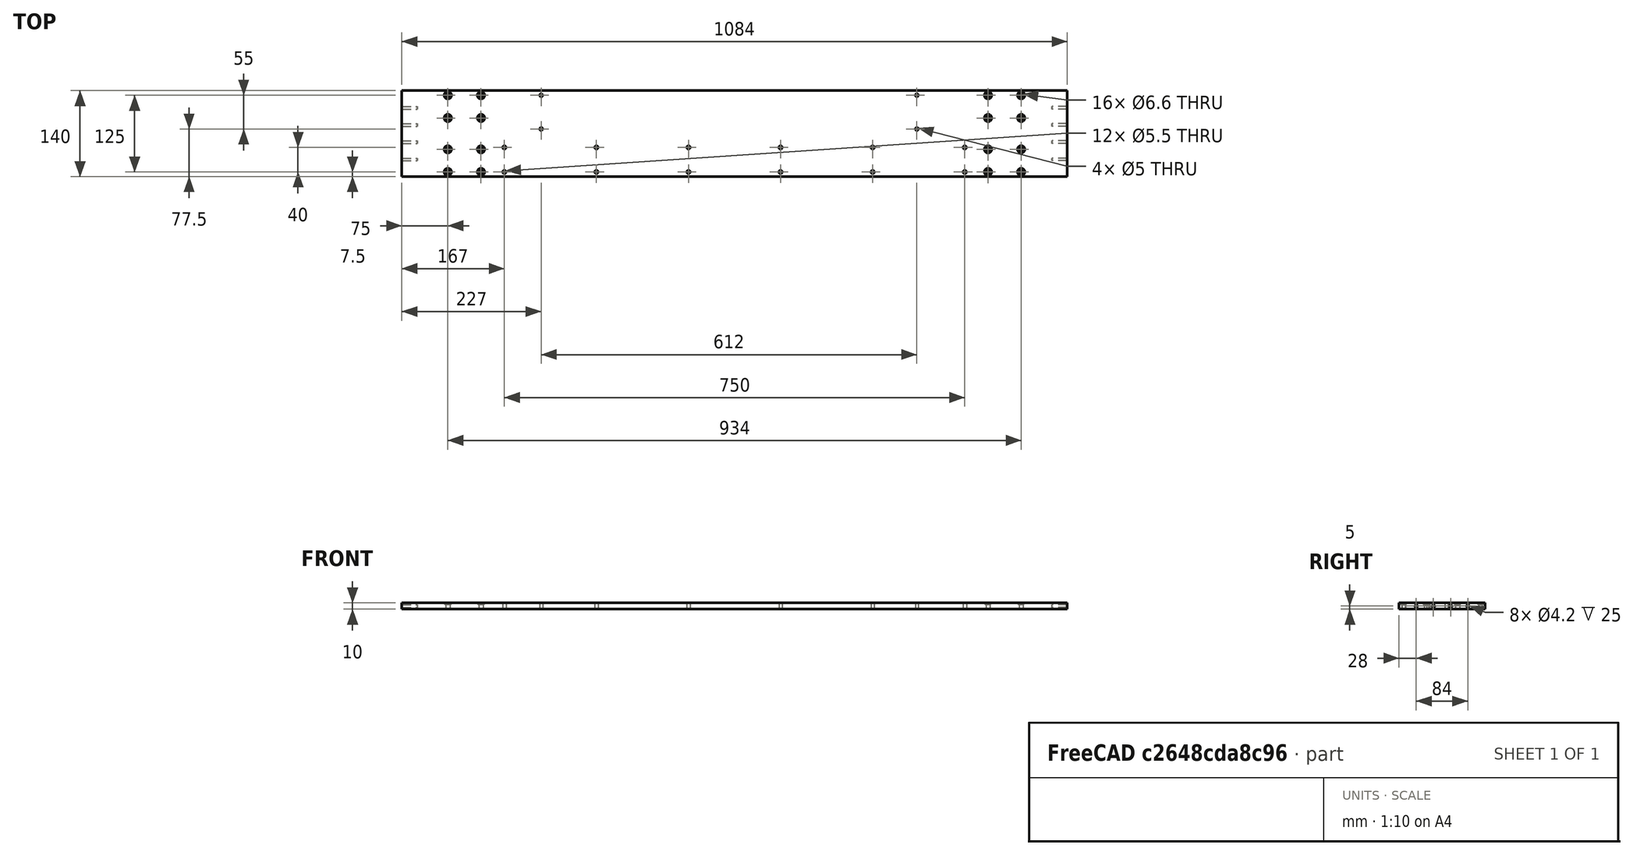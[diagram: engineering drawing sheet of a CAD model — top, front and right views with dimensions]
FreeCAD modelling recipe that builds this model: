
FCSTD DOCUMENT  (FreeCAD 0.17R13528 (Git))
Label: plate1
License: All rights reserved
LicenseURL: http://en.wikipedia.org/wiki/All_rights_reserved
objects: TechDraw::DrawViewDimension×32, PartDesign::LinearPattern×16, Sketcher::SketchObject×13, PartDesign::Hole×12, TechDraw::DrawProjGroupItem×2, PartDesign::Pad×1, PartDesign::Body×1, TechDraw::DrawSVGTemplate×1, TechDraw::DrawProjGroup×1, TechDraw::DrawViewAnnotation×1, TechDraw::DrawPage×1
note: 56 computed .brp shape members not serialized (recipe doc carries the construction recipe); baked Part::Feature solids carry a one-line shape summary decoded from their .brp

FEATURE [Sketcher::SketchObject] Sketch
  MapMode = 5
  Support = -> [XY_Plane]
  sketch-geometry (4):
    g0: LineSegment StartX=0 StartY=0 StartZ=0 EndX=1084 EndY=0 EndZ=0
    g1: LineSegment StartX=1084 StartY=0 StartZ=0 EndX=1084 EndY=140 EndZ=0
    g2: LineSegment StartX=1084 StartY=140 StartZ=0 EndX=0 EndY=140 EndZ=0
    g3: LineSegment StartX=0 StartY=140 StartZ=0 EndX=0 EndY=0 EndZ=0
  constraints (11):
    c: Coincident(g0,g1)
    c: Coincident(g1,g2)
    c: Coincident(g2,g3)
    c: Coincident(g3,g0)
    c: Horizontal(g0)
    c: Horizontal(g2)
    c: Vertical(g1)
    c: Vertical(g3)
    c: Coincident(g0,g-1)
    c: DistanceX(g0,g0) = 1084
    c: DistanceY(g3,g3) = 140
FEATURE [PartDesign::Pad] Pad
  Length = 10
  Length2 = 100
  Profile = -> Sketch
  Type = 0
FEATURE [Sketcher::SketchObject] Sketch001
  MapMode = 5
  Placement = pos=(0,0,10) rot=(0,0,1;0rad)
  Support = -> [Pad]
  sketch-geometry (1):
    g0: Circle CenterX=75 CenterY=7.5 CenterZ=0 NormalX=0 NormalY=0 NormalZ=1 AngleXU=0 Radius=10.4377
  constraints (2):
    c: Distance(g0,g-1) = 7.5
    c: Distance(g0,g-2) = 75
FEATURE [PartDesign::Hole] Hole
  BaseFeature = -> Pad
  Depth = 25
  DepthType = 1
  Diameter = 6.6
  DrillPoint = 0
  DrillPointAngle = 118
  HoleCutCountersinkAngle = 90
  HoleCutDepth = 0
  HoleCutDiameter = 12
  HoleCutType = 2
  ModelActualThread = false
  Profile = -> Sketch001
  Tapered = false
  TaperedAngle = 90
  ThreadAngle = 0
  ThreadClass = 0
  ThreadCutOffInner = 0
  ThreadCutOffOuter = 0
  ThreadDirection = 0
  ThreadFit = 0
  ThreadPitch = 0
  ThreadSize = 7
  ThreadType = 1
  Threaded = false
FEATURE [PartDesign::LinearPattern] LinearPattern
  BaseFeature = -> Hole
  Direction = -> Sketch001 [V_Axis]
  Length = 37
  Occurrences = 2
  Originals = -> [Hole]
FEATURE [PartDesign::LinearPattern] LinearPattern001
  BaseFeature = -> LinearPattern
  Direction = -> Sketch001 [V_Axis]
  Length = 88
  Occurrences = 2
  Originals = -> [Hole]
FEATURE [PartDesign::LinearPattern] LinearPattern002
  BaseFeature = -> LinearPattern001
  Direction = -> Sketch001 [V_Axis]
  Length = 125
  Occurrences = 2
  Originals = -> [Hole]
FEATURE [Sketcher::SketchObject] Sketch002
  MapMode = 5
  Placement = pos=(0,0,10) rot=(0,0,1;0rad)
  Support = -> [LinearPattern002]
  sketch-geometry (1):
    g0: Circle CenterX=129 CenterY=7.5 CenterZ=0 NormalX=0 NormalY=0 NormalZ=1 AngleXU=0 Radius=9.61982
  constraints (2):
    c: Distance(g0,g-1) = 7.5
    c: Distance(g0,g-2) = 129
FEATURE [PartDesign::Hole] Hole001
  BaseFeature = -> LinearPattern002
  Depth = 25
  DepthType = 1
  Diameter = 6.6
  DrillPoint = 0
  DrillPointAngle = 118
  HoleCutCountersinkAngle = 90
  HoleCutDepth = 0
  HoleCutDiameter = 12
  HoleCutType = 2
  ModelActualThread = false
  Profile = -> Sketch002
  Tapered = false
  TaperedAngle = 90
  ThreadAngle = 0
  ThreadClass = 0
  ThreadCutOffInner = 0
  ThreadCutOffOuter = 0
  ThreadDirection = 0
  ThreadFit = 0
  ThreadPitch = 0
  ThreadSize = 7
  ThreadType = 1
  Threaded = false
FEATURE [PartDesign::LinearPattern] LinearPattern003
  BaseFeature = -> Hole001
  Direction = -> Sketch002 [V_Axis]
  Length = 37
  Occurrences = 2
  Originals = -> [Hole001]
FEATURE [PartDesign::LinearPattern] LinearPattern004
  BaseFeature = -> LinearPattern003
  Direction = -> Sketch002 [V_Axis]
  Length = 88
  Occurrences = 2
  Originals = -> [Hole001]
FEATURE [PartDesign::LinearPattern] LinearPattern005
  BaseFeature = -> LinearPattern004
  Direction = -> Sketch002 [V_Axis]
  Length = 125
  Occurrences = 2
  Originals = -> [Hole001]
FEATURE [Sketcher::SketchObject] Sketch003
  MapMode = 5
  Placement = pos=(0,0,10) rot=(0,0,1;0rad)
  Support = -> [LinearPattern005]
  sketch-geometry (1):
    g0: Circle CenterX=167 CenterY=7.5 CenterZ=0 NormalX=0 NormalY=0 NormalZ=1 AngleXU=0 Radius=18.1762
  constraints (2):
    c: Distance(g0,g-1) = 7.5
    c: Distance(g0,g-2) = 167
FEATURE [PartDesign::Hole] Hole002
  BaseFeature = -> LinearPattern005
  Depth = 25
  DepthType = 1
  Diameter = 5.5
  DrillPoint = 0
  DrillPointAngle = 118
  HoleCutCountersinkAngle = 90
  HoleCutDepth = 0
  HoleCutDiameter = 5
  HoleCutType = 0
  ModelActualThread = false
  Profile = -> Sketch003
  Tapered = false
  TaperedAngle = 90
  ThreadAngle = 0
  ThreadClass = 0
  ThreadCutOffInner = 0
  ThreadCutOffOuter = 0
  ThreadDirection = 0
  ThreadFit = 0
  ThreadPitch = 0
  ThreadSize = 6
  ThreadType = 1
  Threaded = false
FEATURE [PartDesign::LinearPattern] LinearPattern006
  BaseFeature = -> Hole002
  Direction = -> Sketch003 [H_Axis]
  Length = 750
  Occurrences = 6
  Originals = -> [Hole002]
FEATURE [Sketcher::SketchObject] Sketch004
  MapMode = 5
  Placement = pos=(0,0,10) rot=(0,0,1;0rad)
  Support = -> [LinearPattern006]
  sketch-geometry (1):
    g0: Circle CenterX=167 CenterY=47.5 CenterZ=0 NormalX=0 NormalY=0 NormalZ=1 AngleXU=0 Radius=11.8826
  constraints (2):
    c: Distance(g0,g-1) = 47.5
    c: Distance(g0,g-2) = 167
FEATURE [PartDesign::Hole] Hole003
  BaseFeature = -> LinearPattern006
  Depth = 25
  DepthType = 1
  Diameter = 5.5
  DrillPoint = 0
  DrillPointAngle = 118
  HoleCutCountersinkAngle = 90
  HoleCutDepth = 0
  HoleCutDiameter = 5
  HoleCutType = 0
  ModelActualThread = false
  Profile = -> Sketch004
  Tapered = false
  TaperedAngle = 90
  ThreadAngle = 0
  ThreadClass = 0
  ThreadCutOffInner = 0
  ThreadCutOffOuter = 0
  ThreadDirection = 0
  ThreadFit = 0
  ThreadPitch = 0
  ThreadSize = 6
  ThreadType = 1
  Threaded = false
FEATURE [PartDesign::LinearPattern] LinearPattern007
  BaseFeature = -> Hole003
  Direction = -> Sketch004 [H_Axis]
  Length = 750
  Occurrences = 6
  Originals = -> [Hole003]
FEATURE [Sketcher::SketchObject] Sketch005
  MapMode = 5
  Placement = pos=(0,0,10) rot=(0,0,1;0rad)
  Support = -> [LinearPattern007]
  sketch-geometry (1):
    g0: Circle CenterX=227 CenterY=132.5 CenterZ=0 NormalX=0 NormalY=0 NormalZ=1 AngleXU=0 Radius=12.3627
  constraints (2):
    c: Distance(g0,g-1) = 132.5
    c: Distance(g0,g-2) = 227
FEATURE [PartDesign::Hole] Hole004
  BaseFeature = -> LinearPattern007
  Depth = 25
  DepthType = 1
  Diameter = 5
  DrillPoint = 0
  DrillPointAngle = 118
  HoleCutCountersinkAngle = 90
  HoleCutDepth = 0
  HoleCutDiameter = 6
  HoleCutType = 0
  ModelActualThread = false
  Profile = -> Sketch005
  Tapered = false
  TaperedAngle = 90
  ThreadAngle = 60
  ThreadClass = 0
  ThreadCutOffInner = 0.108253
  ThreadCutOffOuter = 0.216506
  ThreadDirection = 1
  ThreadFit = 0
  ThreadPitch = 1
  ThreadSize = 7
  ThreadType = 1
  Threaded = true
FEATURE [PartDesign::LinearPattern] LinearPattern008
  BaseFeature = -> Hole004
  Direction = -> Sketch005 [H_Axis]
  Length = 612
  Occurrences = 2
  Originals = -> [Hole004]
FEATURE [Sketcher::SketchObject] Sketch006
  MapMode = 5
  Placement = pos=(0,0,10) rot=(0,0,1;0rad)
  Support = -> [LinearPattern008]
  sketch-geometry (1):
    g0: Circle CenterX=227 CenterY=77.5 CenterZ=0 NormalX=0 NormalY=0 NormalZ=1 AngleXU=0 Radius=12.7181
  constraints (2):
    c: Distance(g0,g-1) = 77.5
    c: Distance(g0,g-2) = 227
FEATURE [PartDesign::Hole] Hole005
  BaseFeature = -> LinearPattern008
  Depth = 25
  DepthType = 1
  Diameter = 5
  DrillPoint = 0
  DrillPointAngle = 118
  HoleCutCountersinkAngle = 90
  HoleCutDepth = 0
  HoleCutDiameter = 6
  HoleCutType = 0
  ModelActualThread = false
  Profile = -> Sketch006
  Tapered = false
  TaperedAngle = 90
  ThreadAngle = 60
  ThreadClass = 0
  ThreadCutOffInner = 0.108253
  ThreadCutOffOuter = 0.216506
  ThreadDirection = 1
  ThreadFit = 0
  ThreadPitch = 1
  ThreadSize = 7
  ThreadType = 1
  Threaded = true
FEATURE [PartDesign::LinearPattern] LinearPattern009
  BaseFeature = -> Hole005
  Direction = -> Sketch006 [H_Axis]
  Length = 612
  Occurrences = 2
  Originals = -> [Hole005]
FEATURE [Sketcher::SketchObject] Sketch007
  MapMode = 5
  Placement = pos=(0,0,10) rot=(0,0,1;0rad)
  Support = -> [LinearPattern009]
  sketch-geometry (1):
    g0: Circle CenterX=1009 CenterY=132.5 CenterZ=0 NormalX=0 NormalY=0 NormalZ=1 AngleXU=0 Radius=17.4662
  constraints (2):
    c: Distance(g0,g-2) = 1009
    c: Distance(g0,g-1) = 132.5
FEATURE [PartDesign::Hole] Hole006
  BaseFeature = -> LinearPattern009
  Depth = 25
  DepthType = 1
  Diameter = 6.6
  DrillPoint = 0
  DrillPointAngle = 118
  HoleCutCountersinkAngle = 90
  HoleCutDepth = 0
  HoleCutDiameter = 12
  HoleCutType = 2
  ModelActualThread = false
  Profile = -> Sketch007
  Tapered = false
  TaperedAngle = 90
  ThreadAngle = 0
  ThreadClass = 0
  ThreadCutOffInner = 0
  ThreadCutOffOuter = 0
  ThreadDirection = 0
  ThreadFit = 0
  ThreadPitch = 0
  ThreadSize = 7
  ThreadType = 1
  Threaded = false
FEATURE [PartDesign::LinearPattern] LinearPattern010
  BaseFeature = -> Hole006
  Direction = -> Sketch007 [H_Axis]
  Length = 54
  Occurrences = 2
  Originals = -> [Hole006]
  Reversed = true
FEATURE [Sketcher::SketchObject] Sketch008
  MapMode = 5
  Placement = pos=(0,0,10) rot=(0,0,1;0rad)
  Support = -> [LinearPattern010]
  sketch-geometry (1):
    g0: Circle CenterX=1009 CenterY=95.5 CenterZ=0 NormalX=0 NormalY=0 NormalZ=1 AngleXU=0 Radius=18.6644
  constraints (2):
    c: Distance(g0,g-2) = 1009
    c: Distance(g0,g-1) = 95.5
FEATURE [PartDesign::Hole] Hole007
  BaseFeature = -> LinearPattern010
  Depth = 25
  DepthType = 1
  Diameter = 6.6
  DrillPoint = 0
  DrillPointAngle = 118
  HoleCutCountersinkAngle = 90
  HoleCutDepth = 0
  HoleCutDiameter = 12
  HoleCutType = 2
  ModelActualThread = false
  Profile = -> Sketch008
  Tapered = false
  TaperedAngle = 90
  ThreadAngle = 0
  ThreadClass = 0
  ThreadCutOffInner = 0
  ThreadCutOffOuter = 0
  ThreadDirection = 0
  ThreadFit = 0
  ThreadPitch = 0
  ThreadSize = 7
  ThreadType = 1
  Threaded = false
FEATURE [PartDesign::LinearPattern] LinearPattern011
  BaseFeature = -> Hole007
  Direction = -> Sketch008 [H_Axis]
  Length = 54
  Occurrences = 2
  Originals = -> [Hole007]
  Reversed = true
FEATURE [Sketcher::SketchObject] Sketch009
  MapMode = 5
  Placement = pos=(0,0,10) rot=(0,0,1;0rad)
  Support = -> [LinearPattern011]
  sketch-geometry (1):
    g0: Circle CenterX=1009 CenterY=7.5 CenterZ=0 NormalX=0 NormalY=0 NormalZ=1 AngleXU=0 Radius=11.8629
  constraints (2):
    c: Distance(g0,g-2) = 1009
    c: Distance(g0,g-1) = 7.5
FEATURE [PartDesign::Hole] Hole008
  BaseFeature = -> LinearPattern011
  Depth = 25
  DepthType = 1
  Diameter = 6.6
  DrillPoint = 0
  DrillPointAngle = 118
  HoleCutCountersinkAngle = 90
  HoleCutDepth = 0
  HoleCutDiameter = 12
  HoleCutType = 2
  ModelActualThread = false
  Profile = -> Sketch009
  Tapered = false
  TaperedAngle = 90
  ThreadAngle = 0
  ThreadClass = 0
  ThreadCutOffInner = 0
  ThreadCutOffOuter = 0
  ThreadDirection = 0
  ThreadFit = 0
  ThreadPitch = 0
  ThreadSize = 7
  ThreadType = 1
  Threaded = false
FEATURE [PartDesign::LinearPattern] LinearPattern012
  BaseFeature = -> Hole008
  Direction = -> Sketch009 [H_Axis]
  Length = 54
  Occurrences = 2
  Originals = -> [Hole008]
  Reversed = true
FEATURE [Sketcher::SketchObject] Sketch010
  MapMode = 5
  Placement = pos=(0,0,10) rot=(0,0,1;0rad)
  Support = -> [LinearPattern012]
  sketch-geometry (1):
    g0: Circle CenterX=1009 CenterY=44.5 CenterZ=0 NormalX=0 NormalY=0 NormalZ=1 AngleXU=0 Radius=7.99747
  constraints (2):
    c: Distance(g0,g-2) = 1009
    c: Distance(g0,g-1) = 44.5
FEATURE [PartDesign::Hole] Hole009
  BaseFeature = -> LinearPattern012
  Depth = 25
  DepthType = 1
  Diameter = 6.6
  DrillPoint = 0
  DrillPointAngle = 118
  HoleCutCountersinkAngle = 90
  HoleCutDepth = 0
  HoleCutDiameter = 12
  HoleCutType = 2
  ModelActualThread = false
  Profile = -> Sketch010
  Tapered = false
  TaperedAngle = 90
  ThreadAngle = 0
  ThreadClass = 0
  ThreadCutOffInner = 0
  ThreadCutOffOuter = 0
  ThreadDirection = 0
  ThreadFit = 0
  ThreadPitch = 0
  ThreadSize = 7
  ThreadType = 1
  Threaded = false
FEATURE [PartDesign::LinearPattern] LinearPattern013
  BaseFeature = -> Hole009
  Direction = -> Sketch010 [H_Axis]
  Length = 54
  Occurrences = 2
  Originals = -> [Hole009]
  Reversed = true
FEATURE [Sketcher::SketchObject] Sketch011
  MapMode = 5
  Placement = pos=(0,0,0) rot=(0.57735,-0.57735,-0.57735;2.0944rad)
  Support = -> [LinearPattern013]
  sketch-geometry (1):
    g0: Circle CenterX=-28 CenterY=5 CenterZ=0 NormalX=0 NormalY=0 NormalZ=1 AngleXU=0 Radius=5.00486
  constraints (2):
    c: Distance(g0,g-1) = 5
    c: Distance(g0,g-2) = 28
FEATURE [PartDesign::Hole] Hole010
  BaseFeature = -> LinearPattern013
  Depth = 25
  DepthType = 0
  Diameter = 4.2
  DrillPoint = 0
  DrillPointAngle = 118
  HoleCutCountersinkAngle = 90
  HoleCutDepth = 0
  HoleCutDiameter = 5
  HoleCutType = 0
  ModelActualThread = false
  Profile = -> Sketch011
  Tapered = false
  TaperedAngle = 90
  ThreadAngle = 60
  ThreadClass = 0
  ThreadCutOffInner = 0.0866025
  ThreadCutOffOuter = 0.173205
  ThreadDirection = 1
  ThreadFit = 0
  ThreadPitch = 0.8
  ThreadSize = 6
  ThreadType = 1
  Threaded = true
FEATURE [PartDesign::LinearPattern] LinearPattern014
  BaseFeature = -> Hole010
  Direction = -> Sketch011 [H_Axis]
  Length = 84
  Occurrences = 4
  Originals = -> [Hole010]
  Reversed = true
FEATURE [Sketcher::SketchObject] Sketch012
  MapMode = 5
  Placement = pos=(1084,0,0) rot=(0.57735,0.57735,0.57735;2.0944rad)
  Support = -> [LinearPattern014]
  sketch-geometry (1):
    g0: Circle CenterX=28 CenterY=5 CenterZ=0 NormalX=0 NormalY=0 NormalZ=1 AngleXU=0 Radius=2.71805
  constraints (2):
    c: Distance(g0,g-2) = 28
    c: Distance(g0,g-1) = 5
FEATURE [PartDesign::Hole] Hole011
  BaseFeature = -> LinearPattern014
  Depth = 25
  DepthType = 0
  Diameter = 4.2
  DrillPoint = 0
  DrillPointAngle = 118
  HoleCutCountersinkAngle = 90
  HoleCutDepth = 0
  HoleCutDiameter = 5
  HoleCutType = 0
  ModelActualThread = false
  Profile = -> Sketch012
  Tapered = false
  TaperedAngle = 90
  ThreadAngle = 60
  ThreadClass = 0
  ThreadCutOffInner = 0.0866025
  ThreadCutOffOuter = 0.173205
  ThreadDirection = 1
  ThreadFit = 0
  ThreadPitch = 0.8
  ThreadSize = 6
  ThreadType = 1
  Threaded = true
FEATURE [PartDesign::LinearPattern] LinearPattern015
  BaseFeature = -> Hole011
  Direction = -> Sketch012 [H_Axis]
  Length = 84
  Occurrences = 4
  Originals = -> [Hole011]
FEATURE [PartDesign::Body] Body
  Group = -> [Sketch,Pad,Sketch001,Hole,LinearPattern,LinearPattern001,LinearPattern002,Sketch002,Hole001,LinearPattern003,LinearPattern004,LinearPattern005,Sketch003,Hole002,LinearPattern006,Sketch004,Hole003,LinearPattern007,Sketch005,Hole004,LinearPattern008,Sketch006,Hole005,LinearPattern009,Sketch007,Hole006,LinearPattern010,Sketch008,Hole007,LinearPattern011,Sketch009,Hole008,LinearPattern012,Sketch010,+8 more]
  Origin = -> Origin
  Tip = -> LinearPattern015
FEATURE [TechDraw::DrawSVGTemplate] Template
  EditableTexts = Designed_by_Name=Lukas Winter; FC-Date=27.08.2018; FC-SC=1:4; FC-SH=1/2; FC-Title=COSI Measure v1.0; Subtitle=Mechanical assembly - plate 1
  Height = 210
  Orientation = 1
  Width = 297
FEATURE [TechDraw::DrawProjGroupItem] ProjItem  label="Front"
  CoarseView = false
  Direction = (0,0,-1)
  Focus = 100
  HardHidden = false
  IsoCount = 0
  IsoHidden = false
  IsoVisible = false
  LockPosition = false
  Perspective = false
  Rotation = 0
  RotationVector = (1,0,0)
  ScaleType = 0
  SeamHidden = false
  SeamVisible = false
  SmoothHidden = false
  SmoothVisible = false
  Source = -> [Body]
  Type = 0
  X = 0
  Y = -32.5
FEATURE [TechDraw::DrawProjGroupItem] ProjItem001  label="Top"
  CoarseView = false
  Direction = (0,-1,0)
  Focus = 100
  HardHidden = false
  IsoCount = 0
  IsoHidden = false
  IsoVisible = false
  LockPosition = false
  Perspective = false
  Rotation = 0
  RotationVector = (1,0,0)
  Scale = 0.125
  ScaleType = 2
  SeamHidden = false
  SeamVisible = false
  SmoothHidden = false
  SmoothVisible = false
  Source = -> [Body]
  Type = 4
  X = 0
  Y = -50
FEATURE [TechDraw::DrawProjGroup] ProjGroup
  Anchor = -> ProjItem
  AutoDistribute = true
  CubeDirs = (6) [(-1.22465e-16,1,-1.83697e-16),(1.98248e-32,-1.83697e-16,-1),(-1,-1.22465e-16,2.67165e-33),(-1.98248e-32,1.83697e-16,1),(1,1.22465e-16,-2.67165e-33),(1.22465e-16,-1,1.83697e-16)]
  CubeRotations = (6) [(1,1.22465e-16,-2.44929e-16),(1,1.22465e-16,-2.44929e-16),(4.89859e-16,1.83697e-16,-1),(-1,-1.22465e-16,2.44929e-16),(-4.89859e-16,-1.83697e-16,1),(1,1.22465e-16,-2.44929e-16)]
  LockPosition = false
  ProjectionType = 0
  Rotation = 0
  Scale = 0.25
  ScaleType = 2
  Source = -> [Body]
  Views = -> [ProjItem,ProjItem001]
  X = 148.275
  Y = 143.647
  spacingX = 15
  spacingY = 15
FEATURE [TechDraw::DrawViewDimension] Dimension
  FormatSpec = %.2f
  LockPosition = false
  MeasureType = 1
  References2D = -> [ProjItem001]
  Rotation = 0
  ScaleType = 0
  Type = 1
  X = -1.86667
  Y = -14
FEATURE [TechDraw::DrawViewDimension] Dimension001
  FormatSpec = %.2f
  LockPosition = false
  MeasureType = 1
  References2D = -> [ProjItem001]
  Rotation = 0
  ScaleType = 0
  Type = 2
  X = -45.1111
  Y = -31.8889
FEATURE [TechDraw::DrawViewDimension] Dimension013
  FormatSpec = %.2f
  LockPosition = false
  MeasureType = 1
  References2D = -> [ProjItem]
  Rotation = 0
  ScaleType = 0
  Type = 1
  X = -107.531
  Y = 28.469
FEATURE [TechDraw::DrawViewDimension] Dimension014
  FormatSpec = %.2f
  LockPosition = false
  MeasureType = 1
  References2D = -> [ProjItem]
  Rotation = 0
  ScaleType = 0
  Type = 1
  X = -124.963
  Y = 36.8148
FEATURE [TechDraw::DrawViewDimension] Dimension020
  FormatSpec = %.2f
  LockPosition = false
  MeasureType = 1
  References2D = -> [ProjItem]
  Rotation = 0
  ScaleType = 0
  Type = 1
  X = -92.7648
  Y = 39.8882
FEATURE [TechDraw::DrawViewDimension] Dimension024
  FormatSpec = %.2f
  LockPosition = false
  MeasureType = 1
  References2D = -> [ProjItem]
  Rotation = 0
  ScaleType = 0
  Type = 2
  X = -90.4522
  Y = -6.07601
FEATURE [TechDraw::DrawViewDimension] Dimension026
  FormatSpec = %.2f
  LockPosition = false
  MeasureType = 1
  References2D = -> [ProjItem]
  Rotation = 0
  ScaleType = 0
  Type = 2
  X = 7.78062
  Y = 7.66924
FEATURE [TechDraw::DrawViewDimension] Dimension027
  FormatSpec = %.2f
  LockPosition = false
  MeasureType = 1
  References2D = -> [ProjItem]
  Rotation = 0
  ScaleType = 0
  Type = 2
  X = 123.504
  Y = -1.77713
FEATURE [TechDraw::DrawViewDimension] Dimension029
  FormatSpec = %.2f
  LockPosition = false
  MeasureType = 1
  References2D = -> [ProjItem]
  Rotation = 0
  ScaleType = 0
  Type = 2
  X = 130.528
  Y = 5.79369
FEATURE [TechDraw::DrawViewAnnotation] Annotation
  Font = osifont
  LineSpace = 80
  LockPosition = false
  MaxWidth = -1
  Rotation = 0
  ScaleType = 0
  Text = The 12 holes in the center top (Front view)  | are for M5 bolts (d=5.5mm). All other holes are | for M6 screws.  | Make countersinks (16x) for the d=6.6mm holes. | Make M6 threads (4x) for the d=5mm holes.
  TextSize = 2.8
  TextStyle = 0
  X = 150.571
  Y = 187.55
FEATURE [TechDraw::DrawViewDimension] Dimension038
  FormatSpec = %.2f
  LockPosition = false
  MeasureType = 1
  References2D = -> [ProjItem]
  Rotation = 0
  ScaleType = 0
  Type = 2
  X = 25.6282
  Y = -0.366117
FEATURE [TechDraw::DrawViewDimension] Dimension039
  FormatSpec = %.2f
  LockPosition = false
  MeasureType = 1
  References2D = -> [ProjItem]
  Rotation = 0
  ScaleType = 0
  Type = 1
  X = 126.382
  Y = 34.3645
FEATURE [TechDraw::DrawViewDimension] Dimension040
  FormatSpec = %.2f
  LockPosition = false
  MeasureType = 1
  References2D = -> [ProjItem]
  Rotation = 0
  ScaleType = 0
  Type = 1
  X = -68.729
  Y = 26.4124
FEATURE [TechDraw::DrawViewDimension] Dimension041
  FormatSpec = %.2f
  LockPosition = false
  MeasureType = 1
  References2D = -> [ProjItem]
  Rotation = 0
  ScaleType = 0
  Type = 1
  X = -38.3406
  Y = 26.4124
FEATURE [TechDraw::DrawViewDimension] Dimension042
  FormatSpec = %.2f
  LockPosition = false
  MeasureType = 1
  References2D = -> [ProjItem]
  Rotation = 0
  ScaleType = 0
  Type = 1
  X = -1.13602
  Y = 26.1284
FEATURE [TechDraw::DrawViewDimension] Dimension043
  FormatSpec = %.2f
  LockPosition = false
  MeasureType = 1
  References2D = -> [ProjItem]
  Rotation = 0
  ScaleType = 0
  Type = 1
  X = 39.4766
  Y = 25.8444
FEATURE [TechDraw::DrawViewDimension] Dimension044
  FormatSpec = %.2f
  LockPosition = false
  MeasureType = 1
  References2D = -> [ProjItem]
  Rotation = 0
  ScaleType = 0
  Type = 1
  X = 76.1131
  Y = 25.5604
FEATURE [TechDraw::DrawViewDimension] Dimension045
  FormatSpec = %.2f
  LockPosition = false
  MeasureType = 1
  References2D = -> [ProjItem]
  Rotation = 0
  ScaleType = 0
  Type = 2
  X = -128.086
  Y = -8.23612
FEATURE [TechDraw::DrawViewDimension] Dimension046
  FormatSpec = %.2f
  LockPosition = false
  MeasureType = 1
  References2D = -> [ProjItem]
  Rotation = 0
  ScaleType = 0
  Type = 2
  X = -132.63
  Y = 6.5321
FEATURE [TechDraw::DrawViewDimension] Dimension047
  FormatSpec = %.2f
  LockPosition = false
  MeasureType = 1
  References2D = -> [ProjItem]
  Rotation = 0
  ScaleType = 0
  Type = 2
  X = -114.454
  Y = 4.82807
FEATURE [TechDraw::DrawViewDimension] Dimension048
  FormatSpec = %.2f
  LockPosition = false
  MeasureType = 1
  References2D = -> [ProjItem]
  Rotation = 0
  ScaleType = 0
  Type = 1
  X = -107.07
  Y = -32.0925
FEATURE [TechDraw::DrawViewDimension] Dimension049
  FormatSpec = %.2f
  LockPosition = false
  MeasureType = 1
  References2D = -> [ProjItem]
  Rotation = 0
  ScaleType = 0
  Type = 1
  X = -0.284004
  Y = -32.3765
FEATURE [TechDraw::DrawViewDimension] Dimension050
  FormatSpec = %.2f
  LockPosition = false
  MeasureType = 1
  References2D = -> [ProjItem]
  Rotation = 0
  ScaleType = 0
  Type = 2
  X = 66.741
  Y = -4.26006
FEATURE [TechDraw::DrawViewDimension] Dimension051
  FormatSpec = %.2f
  LockPosition = false
  MeasureType = 1
  References2D = -> [ProjItem]
  Rotation = 0
  ScaleType = 0
  Type = 2
  X = -72.7051
  Y = -5.11208
FEATURE [TechDraw::DrawViewDimension] Dimension052
  FormatSpec = %.2f
  LockPosition = false
  MeasureType = 1
  References2D = -> [ProjItem]
  Rotation = 0
  ScaleType = 0
  Type = 1
  X = 100.538
  Y = 38.9086
FEATURE [TechDraw::DrawViewDimension] Dimension053
  FormatSpec = %.2f
  LockPosition = false
  MeasureType = 1
  References2D = -> [ProjItem]
  Rotation = 0
  ScaleType = 0
  Type = 1
  X = 113.602
  Y = 28.1164
FEATURE [TechDraw::DrawViewDimension] Dimension054
  FormatSpec = %.2f
  LockPosition = false
  MeasureType = 1
  References2D = -> [ProjItem]
  Rotation = 0
  ScaleType = 0
  Type = 2
  X = 95.9934
  Y = -6.24809
FEATURE [TechDraw::DrawViewDimension] Dimension055
  FormatSpec = %.2f
  LockPosition = false
  MeasureType = 1
  References2D = -> [ProjItem]
  Rotation = 0
  ScaleType = 0
  Type = 5
  X = -10.5024
  Y = -6.00137
FEATURE [TechDraw::DrawViewDimension] Dimension056
  FormatSpec = %.2f
  LockPosition = false
  MeasureType = 1
  References2D = -> [ProjItem]
  Rotation = 0
  ScaleType = 0
  Type = 5
  X = -47.1108
  Y = -11.2526
FEATURE [TechDraw::DrawViewDimension] Dimension057
  FormatSpec = %.2f
  LockPosition = false
  MeasureType = 1
  References2D = -> [ProjItem]
  Rotation = 0
  ScaleType = 0
  Type = 5
  X = 45.0103
  Y = -10.2023
FEATURE [TechDraw::DrawViewDimension] Dimension058
  FormatSpec = %.2f
  LockPosition = false
  MeasureType = 1
  References2D = -> [ProjItem]
  Rotation = 0
  ScaleType = 0
  Type = 5
  X = 112.024
  Y = 0.788901
FEATURE [TechDraw::DrawViewDimension] Dimension059
  FormatSpec = %.2f
  LockPosition = false
  MeasureType = 1
  References2D = -> [ProjItem]
  Rotation = 0
  ScaleType = 0
  Type = 5
  X = -63.3093
  Y = 11.4391
FEATURE [TechDraw::DrawViewDimension] Dimension060
  FormatSpec = %.2f
  LockPosition = false
  MeasureType = 1
  References2D = -> [ProjItem]
  Rotation = 0
  ScaleType = 0
  Type = 2
  X = 128.985
  Y = -19.1308
FEATURE [TechDraw::DrawPage] Page
  KeepUpdated = true
  ProjectionType = 0
  Template = -> Template
  Views = -> [ProjGroup,Dimension,Dimension001,Dimension013,Dimension014,Dimension020,Dimension024,Dimension026,Dimension027,Dimension029,Annotation,Dimension038,Dimension039,Dimension040,Dimension041,Dimension042,Dimension043,Dimension044,Dimension045,Dimension046,Dimension047,Dimension048,Dimension049,Dimension050,Dimension051,Dimension052,Dimension053,Dimension054,Dimension055,Dimension056,Dimension057,+3 more]
